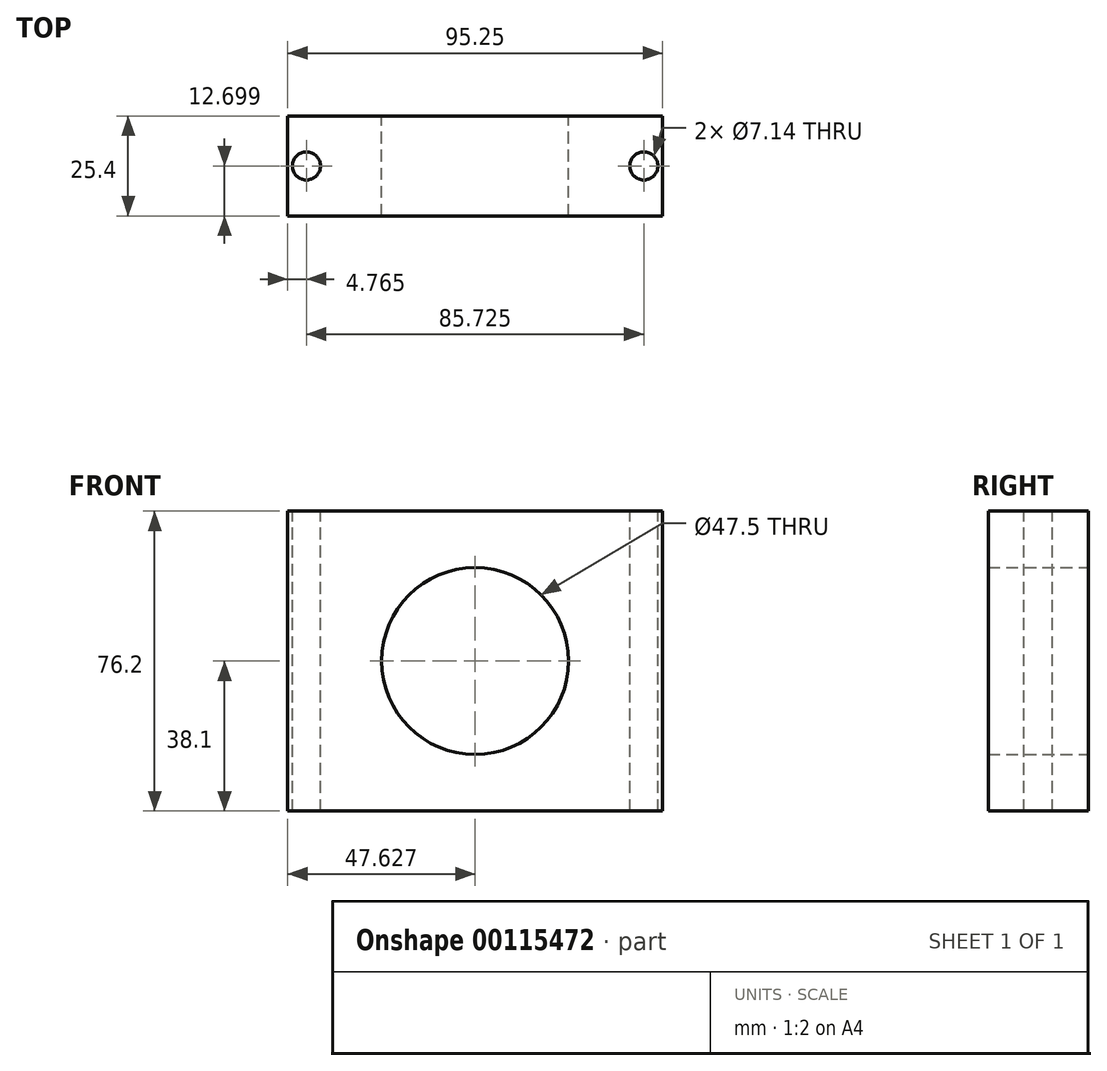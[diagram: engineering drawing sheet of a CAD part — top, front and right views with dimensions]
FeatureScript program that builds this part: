
annotation { "Feature Type Name" : "Feature", "Feature Type Description" : "" }
export const myFeature = defineFeature(function(context is Context, id is Id, definition is map)
    precondition{}
    {
        {
            var Q0;
            Q0=qCreatedBy(makeId("Top.planeOp"),FACE);
            var sketch = newSketch(context, id + "F0", { "sketchPlane" : qUnion([Q0])});
            skLineSegment(sketch, "E0.bottom", {"start": v(-17.76, -7.92) * mm, "end": v(77.5, -7.92) * mm});
            skLineSegment(sketch, "E0.top", {"start": v(-17.76, 17.48) * mm, "end": v(77.5, 17.48) * mm});
            skLineSegment(sketch, "E0.left", {"start": v(-17.76, -7.92) * mm, "end": v(-17.76, 17.48) * mm});
            skLineSegment(sketch, "E0.right", {"start": v(77.5, -7.92) * mm, "end": v(77.5, 17.48) * mm});
            skSolve(sketch);
        }
        {
            var Q0;
            Q0 = qSketchRegion(id + "F0", true);
            extrude(context, id + "F1", {"entities" : qUnion([Q0]), "depth" : 76.2 * mm});
        }
        {
            var Q0;
            Q0=makeQuery(id+"F1.opExtrude","SWEPT_FACE",FACE,{"disambiguationData":[OSD([sQuery(id+"F0.wireOp",EDGE,"E0.top")])]});
            var sketch = newSketch(context, id + "F2", { "sketchPlane" : qUnion([Q0])});
            skPoint(sketch, "E1", {"position": v(17.76, 38.1) * mm});
            skPoint(sketch, "E2", {"position": v(-29.87, 0) * mm});
            skLineSegment(sketch, "E3", {"start": v(17.76, 38.1) * mm, "end": v(-77.5, 38.1) * mm});
            skLineSegment(sketch, "E4", {"start": v(-29.87, 0) * mm, "end": v(-29.87, 76.2) * mm, "construction": true});
            skLineSegment(sketch, "E5", {"start": v(-77.5, 38.1) * mm, "end": v(17.76, 38.1) * mm, "construction": true});
            skCircle(sketch, "E6", {"center": v(-29.87, 38.1) * mm, "radius": 23.75 * mm});
            skSolve(sketch);
        }
        {
            var Q0;
            {var subQ0=sQuery(id+"F2.wireOp",EDGE,"E6");var subQ1=sQuery(id+"F2.wireOp",EDGE,"E3");var subQ2=makeQuery(id+"F2.imprint","INTERSECT",VERTEX,{"disambiguationData":[OD(0.0)],"derivedFrom":[subQ1,subQ0]});Q0=makeQuery(id+"F2.imprint","IMPRINT",FACE,{"disambiguationData":[TD([[makeQuery(id+"F2.imprint","IMPRINT",EDGE,{"disambiguationData":[TD([[subQ2,-1.0]])],"derivedFrom":subQ1}),1.0]])]});}
            var Q1;
            {var subQ0=sQuery(id+"F2.wireOp",EDGE,"E6");var subQ1=sQuery(id+"F2.wireOp",EDGE,"E3");var subQ2=makeQuery(id+"F2.imprint","INTERSECT",VERTEX,{"disambiguationData":[OD(0.0)],"derivedFrom":[subQ1,subQ0]});Q1=makeQuery(id+"F2.imprint","IMPRINT",FACE,{"disambiguationData":[TD([[makeQuery(id+"F2.imprint","IMPRINT",EDGE,{"disambiguationData":[TD([[subQ2,-1.0]])],"derivedFrom":subQ1}),-1.0]])]});}
            extrude(context, id + "F3", {"entities" : qUnion([Q0, Q1]), "operationType" : NewBodyOperationType.REMOVE, "oppositeDirection" : true, "depth" : 25.4 * mm});
        }
        {
            var Q0;
            Q0=makeQuery(id+"F1.opExtrude","CAP_FACE",FACE,{"disambiguationData":[OSD([sQuery(id+"F0.wireOp",EDGE,"E0.bottom"),sQuery(id+"F0.wireOp",EDGE,"E0.top"),sQuery(id+"F0.wireOp",EDGE,"E0.left"),sQuery(id+"F0.wireOp",EDGE,"E0.right")])],"isStart":false});
            var sketch = newSketch(context, id + "F4", { "sketchPlane" : qUnion([Q0])});
            skLineSegment(sketch, "E7", {"start": v(-17.76, 4.78) * mm, "end": v(77.5, 4.78) * mm, "construction": true});
            skLineSegment(sketch, "E8", {"start": v(77.5, 17.48) * mm, "end": v(67.97, 17.48) * mm, "construction": true});
            skLineSegment(sketch, "E9", {"start": v(-17.76, 17.48) * mm, "end": v(-8.23, 17.48) * mm, "construction": true});
            skPoint(sketch, "E10", {"position": v(-13, 17.48) * mm});
            skPoint(sketch, "E11", {"position": v(72.73, 17.48) * mm});
            skLineSegment(sketch, "E12", {"start": v(-13, 17.48) * mm, "end": v(-13, -7.92) * mm, "construction": true});
            skLineSegment(sketch, "E13", {"start": v(72.73, 17.48) * mm, "end": v(72.73, -7.92) * mm, "construction": true});
            skCircle(sketch, "E14", {"center": v(-13, 4.78) * mm, "radius": 3.57 * mm});
            skCircle(sketch, "E15", {"center": v(72.73, 4.78) * mm, "radius": 3.57 * mm});
            skSolve(sketch);
        }
        {
            var Q0;
            Q0=makeQuery(id+"F4.imprint","IMPRINT",FACE,{"disambiguationData":[TD([[makeQuery(id+"F4.imprint","IMPRINT",EDGE,{"derivedFrom":sQuery(id+"F4.wireOp",EDGE,"E15")}),1.0]])]});
            var Q1;
            Q1=makeQuery(id+"F4.imprint","IMPRINT",FACE,{"disambiguationData":[TD([[makeQuery(id+"F4.imprint","IMPRINT",EDGE,{"derivedFrom":sQuery(id+"F4.wireOp",EDGE,"E14")}),1.0]])]});
            extrude(context, id + "F5", {"entities" : qUnion([Q0, Q1]), "operationType" : NewBodyOperationType.REMOVE, "oppositeDirection" : true, "depth" : 76.2 * mm});
        }
    });
